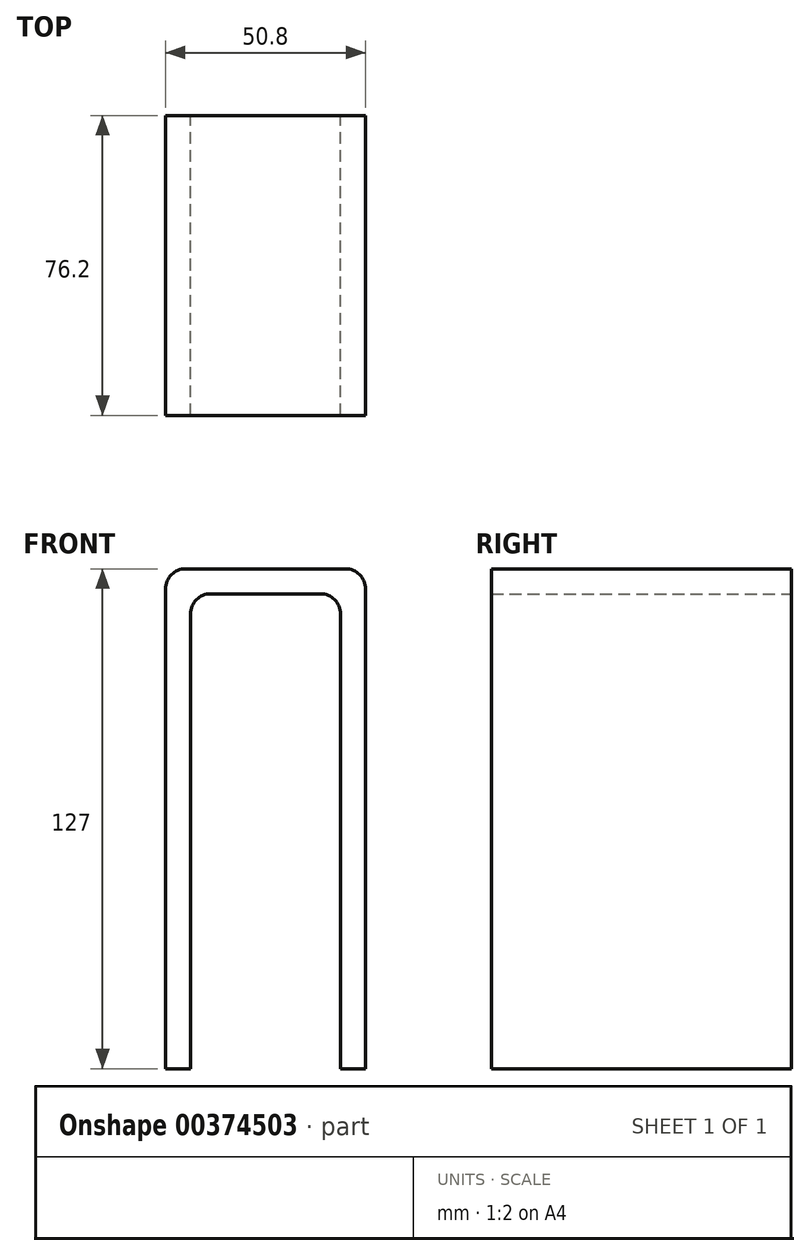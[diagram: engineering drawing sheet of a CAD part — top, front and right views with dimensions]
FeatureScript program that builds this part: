
annotation { "Feature Type Name" : "Feature", "Feature Type Description" : "" }
export const myFeature = defineFeature(function(context is Context, id is Id, definition is map)
    precondition{}
    {
        {
            var Q0;
            Q0=qCreatedBy(makeId("Front.planeOp"),FACE);
            var sketch = newSketch(context, id + "F0", { "sketchPlane" : qUnion([Q0])});
            skLineSegment(sketch, "E0", {"start": v(-31.75, -57.15) * mm, "end": v(-31.75, 69.85) * mm});
            skLineSegment(sketch, "E1", {"start": v(-31.75, 69.85) * mm, "end": v(19.05, 69.85) * mm});
            skLineSegment(sketch, "E2", {"start": v(19.05, 69.85) * mm, "end": v(19.05, -57.15) * mm});
            skLineSegment(sketch, "E3", {"start": v(19.05, -57.15) * mm, "end": v(12.7, -57.15) * mm});
            skLineSegment(sketch, "E4", {"start": v(12.7, -57.15) * mm, "end": v(12.7, 63.5) * mm});
            skLineSegment(sketch, "E5", {"start": v(12.7, 63.5) * mm, "end": v(-25.4, 63.5) * mm});
            skLineSegment(sketch, "E6", {"start": v(-25.4, 63.5) * mm, "end": v(-25.4, -57.15) * mm});
            skLineSegment(sketch, "E7", {"start": v(-25.4, -57.15) * mm, "end": v(-31.75, -57.15) * mm});
            skSolve(sketch);
        }
        {
            var Q0;
            Q0 = qSketchRegion(id + "F0", true);
            extrude(context, id + "F1", {"entities" : qUnion([Q0]), "depth" : 38.1 * mm, "hasSecondDirection" : true, "secondDirectionOppositeDirection" : true, "secondDirectionDepth" : 38.1 * mm});
        }
        {
            var Q0;
            Q0=makeQuery(id+"F1.opExtrude","SWEPT_EDGE",EDGE,{"disambiguationData":[OSD([sQuery(id+"F0.wireOp",EDGE,"E0"),sQuery(id+"F0.wireOp",EDGE,"E1")])]});
            var Q1;
            Q1=makeQuery(id+"F1.opExtrude","SWEPT_EDGE",EDGE,{"disambiguationData":[OSD([sQuery(id+"F0.wireOp",EDGE,"E1"),sQuery(id+"F0.wireOp",EDGE,"E2")])]});
            var Q2;
            Q2=makeQuery(id+"F1.opExtrude","SWEPT_EDGE",EDGE,{"disambiguationData":[OSD([sQuery(id+"F0.wireOp",EDGE,"E5"),sQuery(id+"F0.wireOp",EDGE,"E6")])]});
            var Q3;
            Q3=makeQuery(id+"F1.opExtrude","SWEPT_EDGE",EDGE,{"disambiguationData":[OSD([sQuery(id+"F0.wireOp",EDGE,"E4"),sQuery(id+"F0.wireOp",EDGE,"E5")])]});
            fillet(context, id + "F2", {"entities" : qUnion([Q0, Q1, Q2, Q3]), "radius" : 5.08 * mm, "tangentPropagation" : true, "allowEdgeOverflow" : false});
        }
    });
